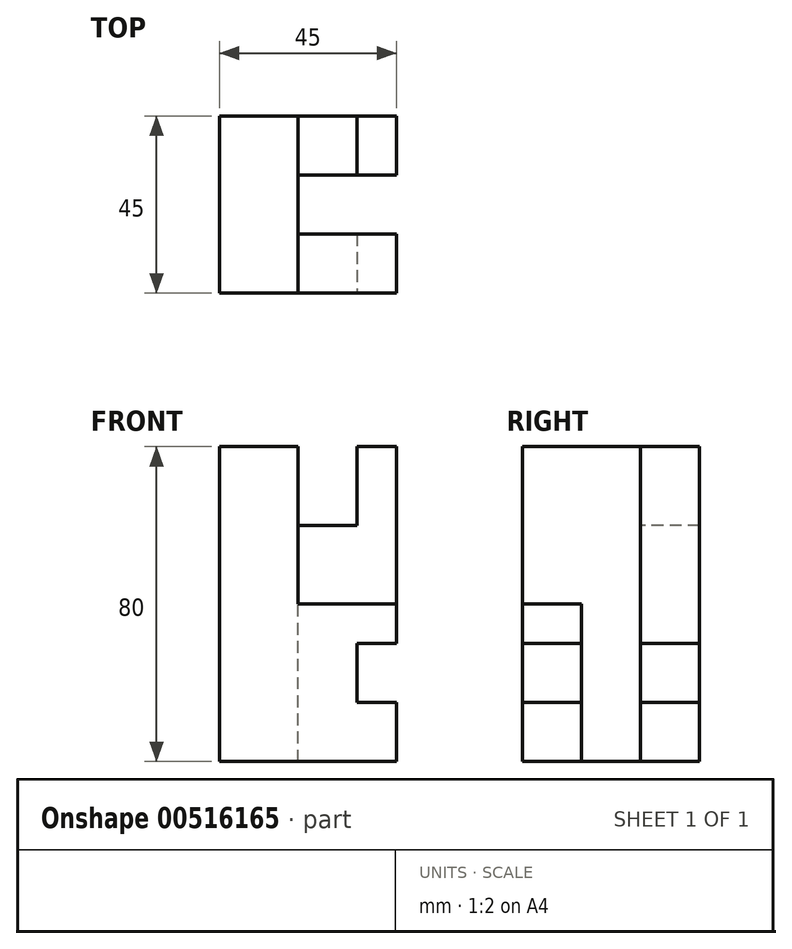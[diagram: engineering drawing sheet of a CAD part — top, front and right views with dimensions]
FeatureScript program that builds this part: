
annotation { "Feature Type Name" : "Feature", "Feature Type Description" : "" }
export const myFeature = defineFeature(function(context is Context, id is Id, definition is map)
    precondition{}
    {
        {
            var Q0;
            Q0=qCreatedBy(makeId("Top.planeOp"),FACE);
            var sketch = newSketch(context, id + "F0", { "sketchPlane" : qUnion([Q0])});
            skLineSegment(sketch, "E0.bottom", {"start": v(22.5, 22.5) * mm, "end": v(-22.5, 22.5) * mm});
            skLineSegment(sketch, "E0.top", {"start": v(22.5, -22.5) * mm, "end": v(-22.5, -22.5) * mm});
            skLineSegment(sketch, "E0.left", {"start": v(22.5, 22.5) * mm, "end": v(22.5, -22.5) * mm});
            skLineSegment(sketch, "E0.right", {"start": v(-22.5, 22.5) * mm, "end": v(-22.5, -22.5) * mm});
            skPoint(sketch, "E0.middle", {"position": v(0, 0) * mm});
            skSolve(sketch);
        }
        {
            var Q0;
            Q0=makeQuery(id+"F0.imprint","IMPRINT",FACE,{"disambiguationData":[TD([[makeQuery(id+"F0.imprint","IMPRINT",EDGE,{"derivedFrom":sQuery(id+"F0.wireOp",EDGE,"E0.bottom")}),1.0]])]});
            extrude(context, id + "F1", {"entities" : qUnion([Q0]), "depth" : 80 * mm, "offsetDistance" : 25 * mm});
        }
        {
            var Q0;
            Q0=makeQuery(id+"F1.opExtrude","CAP_FACE",FACE,{"disambiguationData":[OSD([sQuery(id+"F0.wireOp",EDGE,"E0.bottom"),sQuery(id+"F0.wireOp",EDGE,"E0.top"),sQuery(id+"F0.wireOp",EDGE,"E0.left"),sQuery(id+"F0.wireOp",EDGE,"E0.right")])],"isStart":false});
            var sketch = newSketch(context, id + "F2", { "sketchPlane" : qUnion([Q0])});
            skLineSegment(sketch, "E1", {"start": v(22.5, 22.5) * mm, "end": v(22.5, 7.5) * mm});
            skLineSegment(sketch, "E2", {"start": v(22.5, -22.5) * mm, "end": v(22.5, -7.5) * mm});
            skLineSegment(sketch, "E3", {"start": v(-22.5, -22.5) * mm, "end": v(-2.5, -22.5) * mm});
            skLineSegment(sketch, "E4", {"start": v(-2.5, -22.5) * mm, "end": v(-2.5, -7.5) * mm});
            skLineSegment(sketch, "E5", {"start": v(-2.5, -7.5) * mm, "end": v(22.5, -7.5) * mm});
            skLineSegment(sketch, "E6", {"start": v(-2.5, -22.5) * mm, "end": v(12.5, -22.5) * mm});
            skLineSegment(sketch, "E7", {"start": v(12.5, -22.5) * mm, "end": v(12.5, -7.5) * mm});
            skLineSegment(sketch, "E8", {"start": v(22.5, 7.5) * mm, "end": v(-2.5, 7.5) * mm});
            skLineSegment(sketch, "E9", {"start": v(-2.5, 7.5) * mm, "end": v(-2.5, 22.5) * mm});
            skLineSegment(sketch, "E10", {"start": v(12.5, 7.5) * mm, "end": v(12.5, 22.5) * mm});
            skLineSegment(sketch, "E11", {"start": v(-2.5, 7.5) * mm, "end": v(-2.5, -7.5) * mm});
            skSolve(sketch);
        }
        {
            var Q0;
            Q0=makeQuery(id+"F1.opExtrude","SWEPT_FACE",FACE,{"disambiguationData":[OSD([sQuery(id+"F0.wireOp",EDGE,"E0.top")])]});
            var sketch = newSketch(context, id + "F3", { "sketchPlane" : qUnion([Q0])});
            skLineSegment(sketch, "E12", {"start": v(-22.5, 80) * mm, "end": v(-2.5, 80) * mm});
            skLineSegment(sketch, "E13", {"start": v(-2.5, 80) * mm, "end": v(12.5, 80) * mm});
            skLineSegment(sketch, "E14", {"start": v(22.5, 80) * mm, "end": v(22.5, 60) * mm});
            skLineSegment(sketch, "E15", {"start": v(22.5, 60) * mm, "end": v(12.5, 60) * mm});
            skLineSegment(sketch, "E16", {"start": v(12.5, 60) * mm, "end": v(12.5, 80) * mm});
            skLineSegment(sketch, "E17", {"start": v(12.5, 60) * mm, "end": v(-2.5, 60) * mm});
            skLineSegment(sketch, "E18", {"start": v(-2.5, 60) * mm, "end": v(-2.5, 80) * mm});
            skLineSegment(sketch, "E19", {"start": v(22.5, 80) * mm, "end": v(22.5, 40) * mm});
            skLineSegment(sketch, "E20", {"start": v(22.5, 40) * mm, "end": v(-2.5, 40) * mm});
            skLineSegment(sketch, "E21", {"start": v(-2.5, 40) * mm, "end": v(-2.5, 60) * mm});
            skLineSegment(sketch, "E22", {"start": v(22.5, 80) * mm, "end": v(22.5, 30) * mm});
            skLineSegment(sketch, "E23", {"start": v(22.5, 30) * mm, "end": v(22.5, 15) * mm});
            skLineSegment(sketch, "E24", {"start": v(22.5, 15) * mm, "end": v(22.5, 0) * mm});
            skLineSegment(sketch, "E25", {"start": v(22.5, 0) * mm, "end": v(12.5, 0) * mm});
            skLineSegment(sketch, "E26", {"start": v(12.5, 0) * mm, "end": v(12.5, 30) * mm});
            skLineSegment(sketch, "E27", {"start": v(12.5, 30) * mm, "end": v(22.5, 30) * mm});
            skLineSegment(sketch, "E28", {"start": v(22.5, 15) * mm, "end": v(12.5, 15) * mm});
            skSolve(sketch);
        }
        {
            var Q0;
            {var subQ7=sQuery(id+"F2.wireOp",EDGE,"E11");Q0=makeQuery(id+"F2.imprint","IMPRINT",FACE,{"disambiguationData":[TD([[makeQuery(id+"F2.imprint","IMPRINT",EDGE,{"derivedFrom":subQ7}),1.0]])]});}
            extrude(context, id + "F4", {"entities" : qUnion([Q0]), "operationType" : NewBodyOperationType.REMOVE, "oppositeDirection" : true, "depth" : 80 * mm, "offsetDistance" : 25 * mm});
        }
        {
            var Q0;
            Q0=makeQuery(id+"F3.imprint","IMPRINT",FACE,{"disambiguationData":[TD([[makeQuery(id+"F3.imprint","IMPRINT",EDGE,{"derivedFrom":sQuery(id+"F3.wireOp",EDGE,"E13")}),1.0]])]});
            var Q1;
            Q1=makeQuery(id+"F3.imprint","IMPRINT",FACE,{"disambiguationData":[TD([[makeQuery(id+"F3.imprint","IMPRINT",EDGE,{"derivedFrom":sQuery(id+"F3.wireOp",EDGE,"E23")}),-1.0]])]});
            extrude(context, id + "F5", {"entities" : qUnion([Q0, Q1]), "operationType" : NewBodyOperationType.REMOVE, "oppositeDirection" : true, "depth" : 45 * mm, "offsetDistance" : 25 * mm});
        }
        {
            var Q0;
            {var subQ0=sQuery(id+"F0.wireOp",EDGE,"E0.top");var subQ1=sQuery(id+"F0.wireOp",EDGE,"E0.left");Q0=makeQuery(id+"F5.boolean.opBoolean","SPLIT",FACE,{"disambiguationData":[TD([makeQuery(id+"F4.boolean.opBoolean","COPY",FACE,{"derivedFrom":makeQuery(id+"F4.opExtrude","SWEPT_FACE",FACE,{"disambiguationData":[OSD([sQuery(id+"F2.wireOp",EDGE,"E5")])]})})])],"derivedFrom":makeQuery(id+"F1.opExtrude","CAP_FACE",FACE,{"disambiguationData":[OSD([sQuery(id+"F0.wireOp",EDGE,"E0.bottom"),subQ0,subQ1,sQuery(id+"F0.wireOp",EDGE,"E0.right")])],"isStart":false})});}
            var sketch = newSketch(context, id + "F6", { "sketchPlane" : qUnion([Q0])});
            skLineSegment(sketch, "E29", {"start": v(22.5, -22.5) * mm, "end": v(-2.5, -22.5) * mm});
            skLineSegment(sketch, "E30", {"start": v(22.5, -22.5) * mm, "end": v(22.5, -7.5) * mm});
            skLineSegment(sketch, "E31", {"start": v(22.5, -7.5) * mm, "end": v(-2.5, -7.5) * mm});
            skLineSegment(sketch, "E32", {"start": v(-2.5, -7.5) * mm, "end": v(-2.5, -22.5) * mm});
            skSolve(sketch);
        }
        {
            var Q0;
            Q0 = qSketchRegion(id + "F6", true);
            extrude(context, id + "F7", {"entities" : qUnion([Q0]), "operationType" : NewBodyOperationType.REMOVE, "oppositeDirection" : true, "depth" : 40 * mm, "offsetDistance" : 25 * mm});
        }
        {
            var Q0;
            Q0 = qSketchRegion(id + "F6", true);
            extrude(context, id + "F8", {"entities" : qUnion([Q0]), "operationType" : NewBodyOperationType.REMOVE, "oppositeDirection" : true, "depth" : 40 * mm, "offsetDistance" : 25 * mm});
        }
    });
